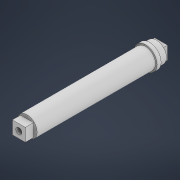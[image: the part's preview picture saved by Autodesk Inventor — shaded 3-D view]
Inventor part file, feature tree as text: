
AUTODESK INVENTOR PART (.ipt)
format: ipt  version: 2021 (Build 250183000, 183)  size: 132,608 bytes
history: native  units: mm
features: extrude x7, sketch x7
ambient origin geometry x8: Origin, YZ Plane, XZ Plane, XY Plane, X Axis, Y Axis, Z Axis, Center Point
bodies: Volumenkörper1 (feature_tree)
feature tree (14):
  extrude  "Extrusion1"  Depth=9.5mm
  extrude  "Extrusion2"  Depth=3.5mm
  extrude  "Extrusion7"  Depth=5.0mm
  extrude  "Extrusion8"  Depth=3.0mm
  extrude  "Extrusion9"  Depth=9.5mm
  extrude  "Extrusion10"  Depth=6.0mm TaperAngle=0.0deg
  extrude  "Extrusion11"  Depth=5.0mm TaperAngle=0.0deg
  sketch  "Skizze1"  dims[d0=9.5mm d1=9.5mm]
  sketch  "Skizze2"  dims[d2=3.5mm d3=0.0mm d4=14.8mm]
  sketch  "Skizze7"  dims[d5=5.0mm d6=0.0mm d20=17.0mm]
  sketch  "Skizze8"  dims[d21=3.0mm d22=0.0mm d23=14.8mm]
  sketch  "Skizze9"  dims[d24=87.0mm d25=0.0mm d26=9.5mm]
  sketch  "Skizze10"  dims[d27=9.5mm d28=6.0mm d29=0.0mm]
  sketch  "Skizze11"  dims[d30=4.5mm d31=5.0mm d32=0.0mm d33=4.5mm d34=5.0mm d35=0.0mm]
